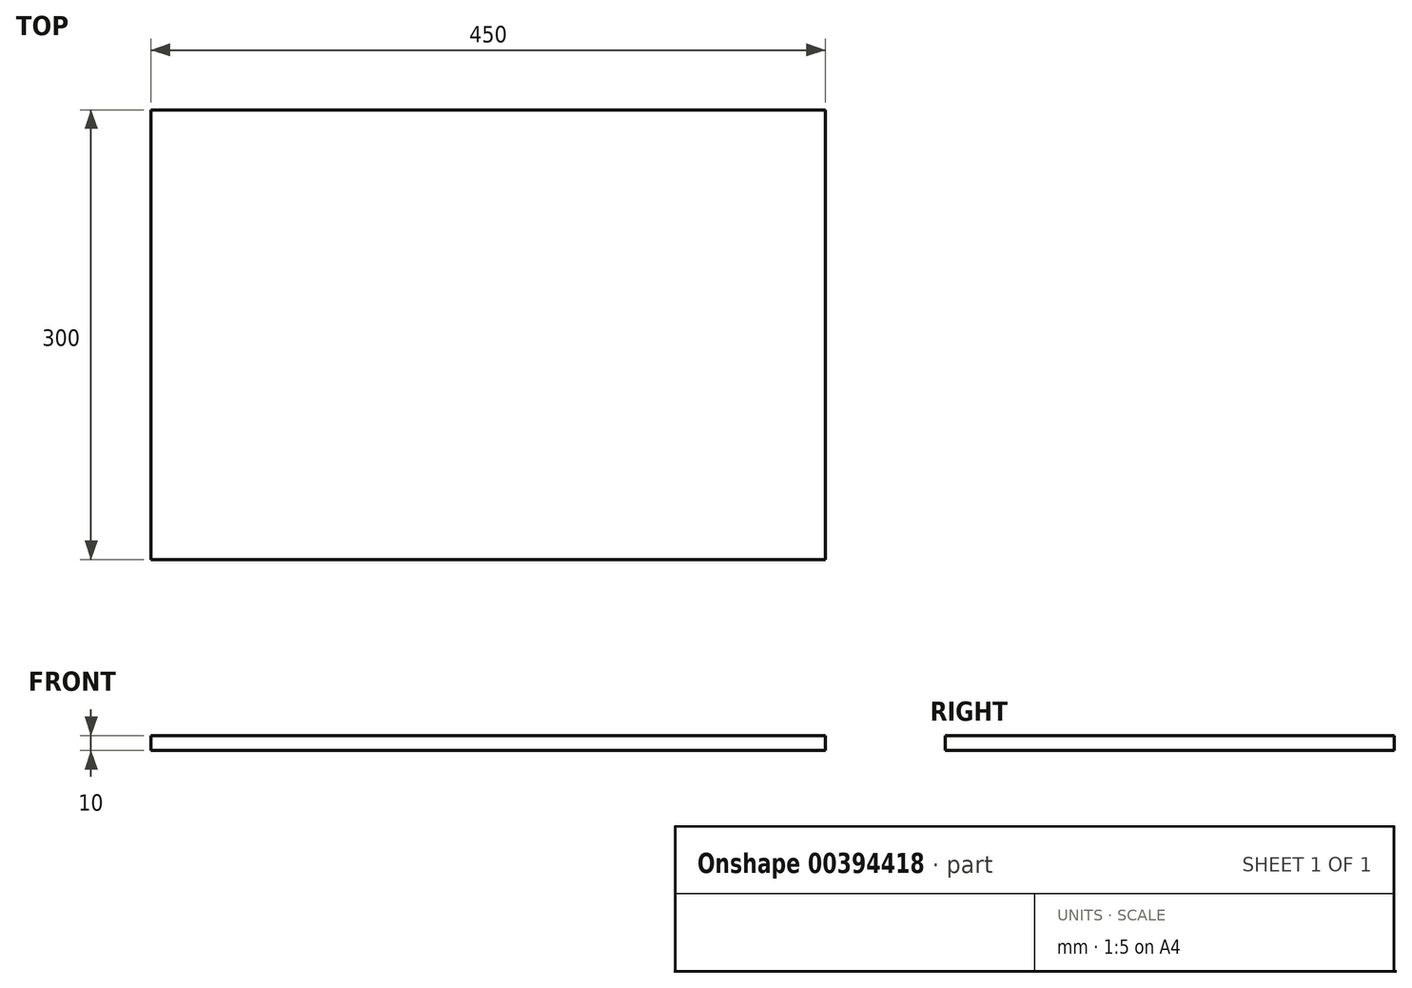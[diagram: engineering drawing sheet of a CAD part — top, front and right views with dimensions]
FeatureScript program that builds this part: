
annotation { "Feature Type Name" : "Feature", "Feature Type Description" : "" }
export const myFeature = defineFeature(function(context is Context, id is Id, definition is map)
    precondition{}
    {
        {
            var Q0;
            Q0=qCreatedBy(makeId("Top.planeOp"),FACE);
            var sketch = newSketch(context, id + "F0", { "sketchPlane" : qUnion([Q0])});
            skLineSegment(sketch, "E0.bottom", {"start": v(0, 300) * mm, "end": v(450, 300) * mm});
            skLineSegment(sketch, "E0.top", {"start": v(0, 0) * mm, "end": v(450, 0) * mm});
            skLineSegment(sketch, "E0.left", {"start": v(0, 300) * mm, "end": v(0, 0) * mm});
            skLineSegment(sketch, "E0.right", {"start": v(450, 300) * mm, "end": v(450, 0) * mm});
            skSolve(sketch);
        }
        {
            var Q0;
            Q0=makeQuery(id+"F0.imprint","IMPRINT",FACE,{"disambiguationData":[TD([[makeQuery(id+"F0.imprint","IMPRINT",EDGE,{"derivedFrom":sQuery(id+"F0.wireOp",EDGE,"E0.bottom")}),-1.0]])]});
            extrude(context, id + "F1", {"entities" : qUnion([Q0]), "depth" : 10 * mm, "offsetDistance" : 25 * mm});
        }
    });
